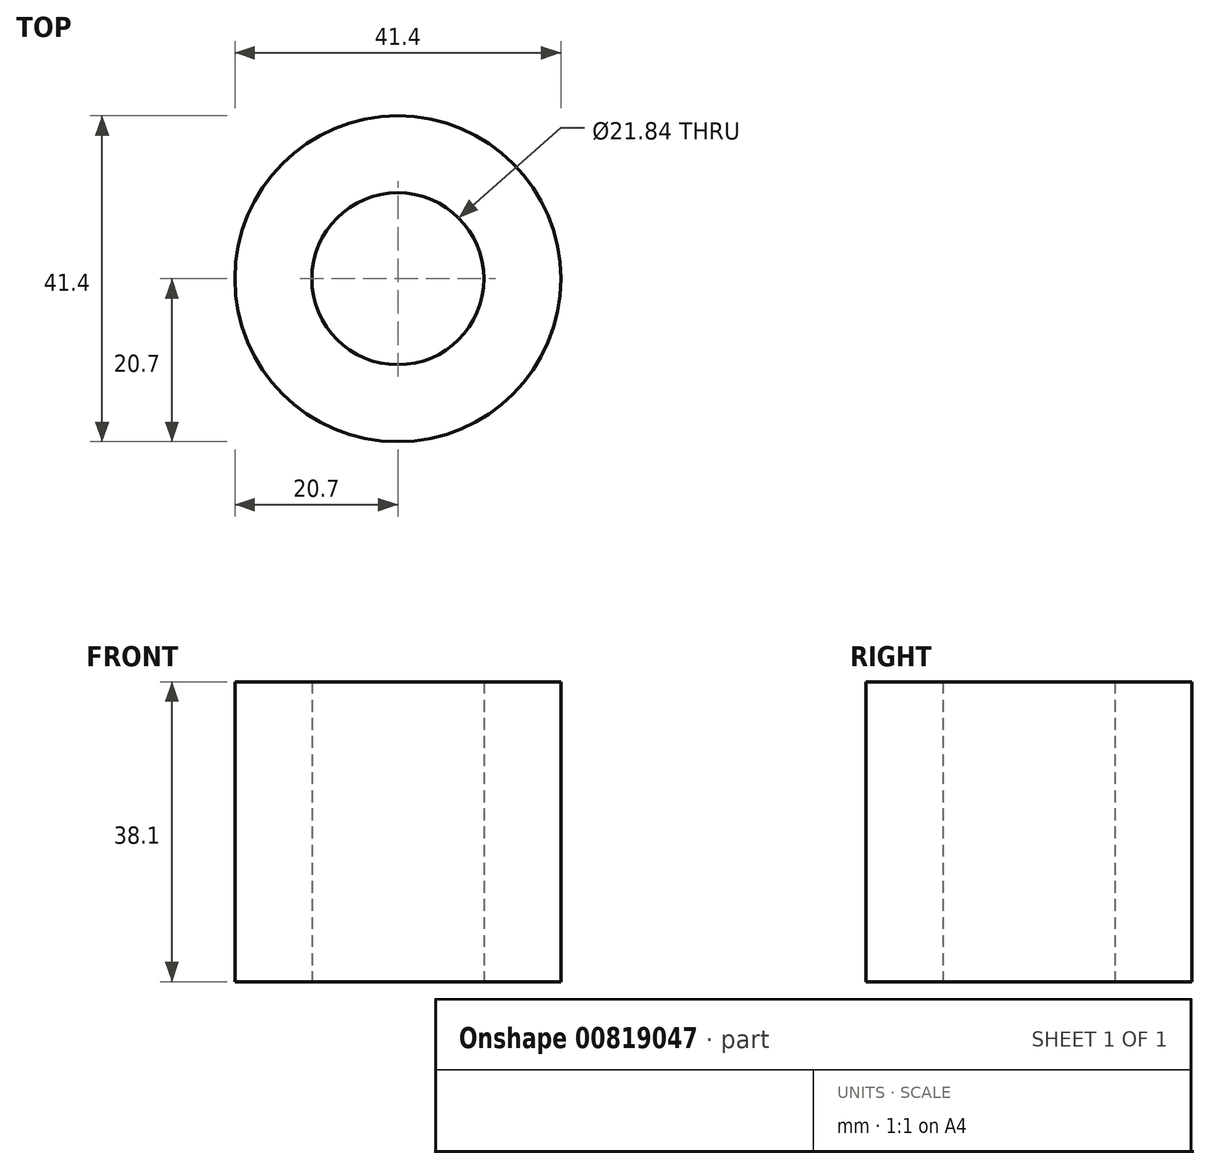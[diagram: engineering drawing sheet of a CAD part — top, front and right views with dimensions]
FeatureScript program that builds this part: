
annotation { "Feature Type Name" : "Feature", "Feature Type Description" : "" }
export const myFeature = defineFeature(function(context is Context, id is Id, definition is map)
    precondition{}
    {
        {
            var Q0;
            Q0=qCreatedBy(makeId("Top.planeOp"),FACE);
            var sketch = newSketch(context, id + "F0", { "sketchPlane" : qUnion([Q0])});
            skCircle(sketch, "E0", {"center": v(0, 0) * mm, "radius": 10.92 * mm});
            skCircle(sketch, "E1", {"center": v(0, 0) * mm, "radius": 20.7 * mm});
            skSolve(sketch);
        }
        {
            var Q0;
            Q0 = qSketchRegion(id + "F0", true);
            extrude(context, id + "F1", {"entities" : qUnion([Q0]), "depth" : 38.1 * mm, "offsetDistance" : 25.4 * mm});
        }
    });
